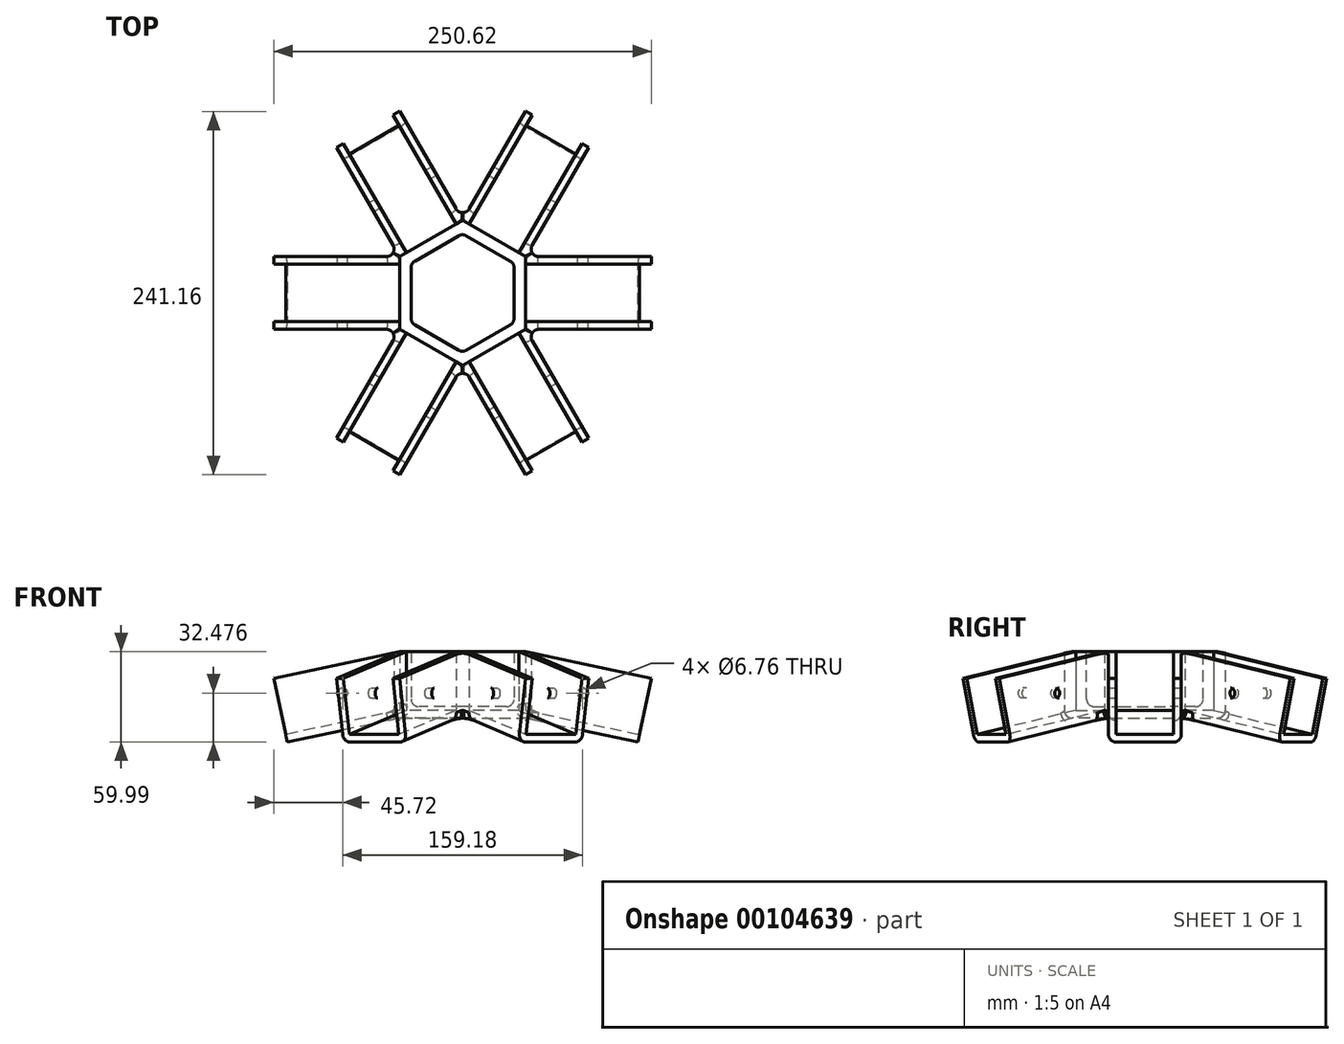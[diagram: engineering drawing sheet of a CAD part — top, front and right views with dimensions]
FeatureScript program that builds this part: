
annotation { "Feature Type Name" : "Feature", "Feature Type Description" : "" }
export const myFeature = defineFeature(function(context is Context, id is Id, definition is map)
    precondition{}
    {
        {
            var Q0;
            Q0=qCreatedBy(makeId("Top.planeOp"),FACE);
            var sketch = newSketch(context, id + "F0", { "sketchPlane" : qUnion([Q0])});
            skCircle(sketch, "E0.cCircle", {"center": v(0, 0) * mm, "radius": 41.8 * mm, "construction": true});
            skLineSegment(sketch, "E0.0", {"start": v(41.8, 24.13) * mm, "end": v(41.8, -24.13) * mm});
            skLineSegment(sketch, "E0.1", {"start": v(41.8, -24.13) * mm, "end": v(0, -48.26) * mm});
            skLineSegment(sketch, "E0.2", {"start": v(0, -48.26) * mm, "end": v(-41.8, -24.13) * mm});
            skLineSegment(sketch, "E0.3", {"start": v(-41.8, -24.13) * mm, "end": v(-41.8, 24.13) * mm});
            skLineSegment(sketch, "E0.4", {"start": v(-41.8, 24.13) * mm, "end": v(0, 48.26) * mm});
            skLineSegment(sketch, "E0.5", {"start": v(0, 48.26) * mm, "end": v(41.8, 24.13) * mm});
            skPoint(sketch, "E0.0.midPoint", {"position": v(41.8, 0) * mm});
            skSolve(sketch);
        }
        {
            var Q0;
            Q0=qSketchRegion(id+"F0",true);
            extrude(context, id + "F1", {"entities" : qUnion([Q0]), "depth" : 44.15 * mm});
        }
        {
            var Q0;
            Q0=qCreatedBy(makeId("Front.planeOp"),FACE);
            var sketch = newSketch(context, id + "F2", { "sketchPlane" : qUnion([Q0])});
            skLineSegment(sketch, "E1", {"start": v(41.8, 0) * mm, "end": v(116.33, -15.84) * mm});
            skLineSegment(sketch, "E2", {"start": v(116.33, -15.84) * mm, "end": v(125.3, 26.4) * mm});
            skLineSegment(sketch, "E3", {"start": v(125.3, 26.4) * mm, "end": v(41.8, 44.15) * mm});
            skLineSegment(sketch, "E4", {"start": v(41.8, 44.15) * mm, "end": v(41.8, 0) * mm});
            skSolve(sketch);
        }
        {
            var Q0;
            Q0=makeQuery(id+"F2.imprint","IMPRINT",FACE,{"disambiguationData":[TD([[makeQuery(id+"F2.imprint","IMPRINT",EDGE,{"derivedFrom":sQuery(id+"F2.wireOp",EDGE,"E1")}),1.0]])]});
            extrude(context, id + "F3", {"entities" : qUnion([Q0]), "endBound" : BoundingType.SYMMETRIC, "depth" : 48.26 * mm});
        }
        {
            var Q0;
            Q0=makeQuery(id+"F3.opExtrude","SWEPT_FACE",FACE,{"disambiguationData":[OSD([sQuery(id+"F2.wireOp",EDGE,"E3")])]});
            var Q1;
            Q1=makeQuery(id+"F3.opExtrude","SWEPT_FACE",FACE,{"disambiguationData":[OSD([sQuery(id+"F2.wireOp",EDGE,"E2")])]});
            var Q2;
            Q2=makeQuery(id+"F3.opExtrude","SWEPT_FACE",FACE,{"disambiguationData":[OSD([sQuery(id+"F2.wireOp",EDGE,"E4")])]});
            shell(context, id + "F4", {"entities" : qUnion([Q0, Q1, Q2]), "thickness" : 5.08 * mm});
        }
        {
            var Q0;
            Q0=makeQuery(id+"F3.opExtrude","CAP_FACE",FACE,{"disambiguationData":[OSD([sQuery(id+"F2.wireOp",EDGE,"E1"),sQuery(id+"F2.wireOp",EDGE,"E2"),sQuery(id+"F2.wireOp",EDGE,"E3"),sQuery(id+"F2.wireOp",EDGE,"E4")])],"isStart":false});
            var sketch = newSketch(context, id + "F5", { "sketchPlane" : qUnion([Q0])});
            skPoint(sketch, "E5", {"position": v(79.59, 16.64) * mm});
            skLineSegment(sketch, "E6", {"start": v(41.8, 44.15) * mm, "end": v(117.39, -10.87) * mm, "construction": true});
            skSolve(sketch);
        }
        {
            var Q0;
            Q0=sQuery(id+"F5.wireOp",VERTEX,"E5");
            var Q1;
            Q1=makeQuery(id+"F3.opExtrude","SWEPT_BODY",BODY,{"disambiguationData":[OSD([sQuery(id+"F2.wireOp",EDGE,"E1"),sQuery(id+"F2.wireOp",EDGE,"E2"),sQuery(id+"F2.wireOp",EDGE,"E3"),sQuery(id+"F2.wireOp",EDGE,"E4")])]});
            hole(context, id + "F6", {"style" : HoleStyle.SIMPLE, "endStyle" : HoleEndStyle.THROUGH, "standardTappedOrClearance" : lookupTablePath({ "standard" : "ANSI", "fit" : "Normal (ASME)", "size" : "1/4", "type" : "Clearance" }), "standardBlindInLast" : lookupTablePath({ "fit" : "Free", "standard" : "ANSI", "size" : "1/4", "type" : "Clearance" }), "holeDiameter" : 6.76 * mm, "locations" : qUnion([Q0]), "scope" : qUnion([Q1]), "isTappedThrough" : true});
        }
        {
            var Q0;
            Q0=qCreatedBy(makeId("Front.planeOp"),FACE);
            var sketch = newSketch(context, id + "F7", { "sketchPlane" : qUnion([Q0])});
            skLineSegment(sketch, "E7", {"start": v(0, 0) * mm, "end": v(0, 66.69) * mm, "construction": true});
            skSolve(sketch);
        }
        {
            var Q0;
            Q0=makeQuery(id+"F1.opExtrude","CAP_FACE",FACE,{"disambiguationData":[OSD([sQuery(id+"F0.wireOp",EDGE,"E0.0"),sQuery(id+"F0.wireOp",EDGE,"E0.1"),sQuery(id+"F0.wireOp",EDGE,"E0.2"),sQuery(id+"F0.wireOp",EDGE,"E0.3"),sQuery(id+"F0.wireOp",EDGE,"E0.4"),sQuery(id+"F0.wireOp",EDGE,"E0.5")])],"isStart":false});
            shell(context, id + "F8", {"entities" : qUnion([Q0]), "thickness" : 7.62 * mm});
        }
        {
            var Q0;
            Q0=makeQuery(id+"F3.opExtrude","SWEPT_BODY",BODY,{"disambiguationData":[OSD([sQuery(id+"F2.wireOp",EDGE,"E1"),sQuery(id+"F2.wireOp",EDGE,"E2"),sQuery(id+"F2.wireOp",EDGE,"E3"),sQuery(id+"F2.wireOp",EDGE,"E4")])]});
            var Q1;
            Q1=sQuery(id+"F7.wireOp",EDGE,"E7");
            circularPattern(context, id + "F9", {"entities" : qUnion([Q0]), "axis" : qUnion([Q1]), "angle" : 60 * degree, "instanceCount" : 6});
        }
        {
            var Q0;
            Q0=makeQuery(id+"F9.opPattern","COPY",BODY,{"derivedFrom":makeQuery(id+"F3.opExtrude","SWEPT_BODY",BODY,{"disambiguationData":[OSD([sQuery(id+"F2.wireOp",EDGE,"E1"),sQuery(id+"F2.wireOp",EDGE,"E2"),sQuery(id+"F2.wireOp",EDGE,"E3"),sQuery(id+"F2.wireOp",EDGE,"E4")])]}),"instanceName":"3"});
            var Q1;
            Q1=makeQuery(id+"F9.opPattern","COPY",BODY,{"derivedFrom":makeQuery(id+"F3.opExtrude","SWEPT_BODY",BODY,{"disambiguationData":[OSD([sQuery(id+"F2.wireOp",EDGE,"E1"),sQuery(id+"F2.wireOp",EDGE,"E2"),sQuery(id+"F2.wireOp",EDGE,"E3"),sQuery(id+"F2.wireOp",EDGE,"E4")])]}),"instanceName":"2"});
            var Q2;
            Q2=makeQuery(id+"F9.opPattern","COPY",BODY,{"derivedFrom":makeQuery(id+"F3.opExtrude","SWEPT_BODY",BODY,{"disambiguationData":[OSD([sQuery(id+"F2.wireOp",EDGE,"E1"),sQuery(id+"F2.wireOp",EDGE,"E2"),sQuery(id+"F2.wireOp",EDGE,"E3"),sQuery(id+"F2.wireOp",EDGE,"E4")])]}),"instanceName":"1"});
            var Q3;
            Q3=makeQuery(id+"F3.opExtrude","SWEPT_BODY",BODY,{"disambiguationData":[OSD([sQuery(id+"F2.wireOp",EDGE,"E1"),sQuery(id+"F2.wireOp",EDGE,"E2"),sQuery(id+"F2.wireOp",EDGE,"E3"),sQuery(id+"F2.wireOp",EDGE,"E4")])]});
            var Q4;
            Q4=makeQuery(id+"F9.opPattern","COPY",BODY,{"derivedFrom":makeQuery(id+"F3.opExtrude","SWEPT_BODY",BODY,{"disambiguationData":[OSD([sQuery(id+"F2.wireOp",EDGE,"E1"),sQuery(id+"F2.wireOp",EDGE,"E2"),sQuery(id+"F2.wireOp",EDGE,"E3"),sQuery(id+"F2.wireOp",EDGE,"E4")])]}),"instanceName":"5"});
            var Q5;
            Q5=makeQuery(id+"F9.opPattern","COPY",BODY,{"derivedFrom":makeQuery(id+"F3.opExtrude","SWEPT_BODY",BODY,{"disambiguationData":[OSD([sQuery(id+"F2.wireOp",EDGE,"E1"),sQuery(id+"F2.wireOp",EDGE,"E2"),sQuery(id+"F2.wireOp",EDGE,"E3"),sQuery(id+"F2.wireOp",EDGE,"E4")])]}),"instanceName":"4"});
            var Q6;
            Q6=makeQuery(id+"F1.opExtrude","SWEPT_BODY",BODY,{"disambiguationData":[OSD([sQuery(id+"F0.wireOp",EDGE,"E0.0"),sQuery(id+"F0.wireOp",EDGE,"E0.1"),sQuery(id+"F0.wireOp",EDGE,"E0.2"),sQuery(id+"F0.wireOp",EDGE,"E0.3"),sQuery(id+"F0.wireOp",EDGE,"E0.4"),sQuery(id+"F0.wireOp",EDGE,"E0.5")])]});
            booleanBodies(context, id + "F10", {"operationType" : BooleanOperationType.UNION, "tools" : qUnion([Q0, Q1, Q2, Q3, Q4, Q5, Q6])});
        }
        {
            var Q0;
            Q0=makeQuery(id+"F8.opShell","OFFSET_EDGE",EDGE,{"disambiguationData":[OSD([sQuery(id+"F0.wireOp",EDGE,"E0.4"),sQuery(id+"F0.wireOp",EDGE,"E0.5")])]});
            var Q1;
            Q1=makeQuery(id+"F8.opShell","OFFSET_EDGE",EDGE,{"disambiguationData":[OSD([sQuery(id+"F0.wireOp",EDGE,"E0.0"),sQuery(id+"F0.wireOp",EDGE,"E0.5")])]});
            var Q2;
            Q2=makeQuery(id+"F8.opShell","OFFSET_EDGE",EDGE,{"disambiguationData":[OSD([sQuery(id+"F0.wireOp",EDGE,"E0.0"),sQuery(id+"F0.wireOp",EDGE,"E0.1")])]});
            var Q3;
            Q3=makeQuery(id+"F8.opShell","OFFSET_EDGE",EDGE,{"disambiguationData":[OSD([sQuery(id+"F0.wireOp",EDGE,"E0.1"),sQuery(id+"F0.wireOp",EDGE,"E0.2")])]});
            var Q4;
            Q4=makeQuery(id+"F8.opShell","OFFSET_EDGE",EDGE,{"disambiguationData":[OSD([sQuery(id+"F0.wireOp",EDGE,"E0.2"),sQuery(id+"F0.wireOp",EDGE,"E0.3")])]});
            var Q5;
            Q5=makeQuery(id+"F8.opShell","OFFSET_EDGE",EDGE,{"disambiguationData":[OSD([sQuery(id+"F0.wireOp",EDGE,"E0.3"),sQuery(id+"F0.wireOp",EDGE,"E0.4")])]});
            fillet(context, id + "F11", {"entities" : qUnion([Q0, Q1, Q2, Q3, Q4, Q5]), "radius" : 5.08 * mm, "tangentPropagation" : true, "allowEdgeOverflow" : false});
        }
        {
            var Q0;
            {var subQ0=sQuery(id+"F2.wireOp",EDGE,"E4");Q0=makeQuery(id+"F10.opBoolean","MERGE",EDGE,{"derivedFrom":[makeQuery(id+"F1.opExtrude","SWEPT_EDGE",EDGE,{"disambiguationData":[OSD([sQuery(id+"F0.wireOp",EDGE,"E0.1"),sQuery(id+"F0.wireOp",EDGE,"E0.2")])]}),makeQuery(id+"F9.opPattern","COPY",EDGE,{"derivedFrom":makeQuery(id+"F3.opExtrude","CAP_EDGE",EDGE,{"disambiguationData":[OSD([subQ0])],"isStart":true}),"instanceName":"4"}),makeQuery(id+"F9.opPattern","COPY",EDGE,{"derivedFrom":makeQuery(id+"F3.opExtrude","CAP_EDGE",EDGE,{"disambiguationData":[OSD([subQ0])],"isStart":false}),"instanceName":"5"})]});}
            var Q1;
            {var subQ0=sQuery(id+"F2.wireOp",EDGE,"E4");Q1=makeQuery(id+"F10.opBoolean","MERGE",EDGE,{"derivedFrom":[makeQuery(id+"F1.opExtrude","SWEPT_EDGE",EDGE,{"disambiguationData":[OSD([sQuery(id+"F0.wireOp",EDGE,"E0.0"),sQuery(id+"F0.wireOp",EDGE,"E0.1")])]}),makeQuery(id+"F3.opExtrude","CAP_EDGE",EDGE,{"disambiguationData":[OSD([subQ0])],"isStart":false}),makeQuery(id+"F9.opPattern","COPY",EDGE,{"derivedFrom":makeQuery(id+"F3.opExtrude","CAP_EDGE",EDGE,{"disambiguationData":[OSD([subQ0])],"isStart":true}),"instanceName":"5"})]});}
            var Q2;
            {var subQ0=sQuery(id+"F2.wireOp",EDGE,"E4");Q2=makeQuery(id+"F10.opBoolean","MERGE",EDGE,{"derivedFrom":[makeQuery(id+"F1.opExtrude","SWEPT_EDGE",EDGE,{"disambiguationData":[OSD([sQuery(id+"F0.wireOp",EDGE,"E0.0"),sQuery(id+"F0.wireOp",EDGE,"E0.5")])]}),makeQuery(id+"F3.opExtrude","CAP_EDGE",EDGE,{"disambiguationData":[OSD([subQ0])],"isStart":true}),makeQuery(id+"F9.opPattern","COPY",EDGE,{"derivedFrom":makeQuery(id+"F3.opExtrude","CAP_EDGE",EDGE,{"disambiguationData":[OSD([subQ0])],"isStart":false}),"instanceName":"1"})]});}
            var Q3;
            {var subQ0=sQuery(id+"F2.wireOp",EDGE,"E4");Q3=makeQuery(id+"F10.opBoolean","MERGE",EDGE,{"derivedFrom":[makeQuery(id+"F1.opExtrude","SWEPT_EDGE",EDGE,{"disambiguationData":[OSD([sQuery(id+"F0.wireOp",EDGE,"E0.4"),sQuery(id+"F0.wireOp",EDGE,"E0.5")])]}),makeQuery(id+"F9.opPattern","COPY",EDGE,{"derivedFrom":makeQuery(id+"F3.opExtrude","CAP_EDGE",EDGE,{"disambiguationData":[OSD([subQ0])],"isStart":true}),"instanceName":"1"}),makeQuery(id+"F9.opPattern","COPY",EDGE,{"derivedFrom":makeQuery(id+"F3.opExtrude","CAP_EDGE",EDGE,{"disambiguationData":[OSD([subQ0])],"isStart":false}),"instanceName":"2"})]});}
            var Q4;
            {var subQ0=sQuery(id+"F2.wireOp",EDGE,"E4");Q4=makeQuery(id+"F10.opBoolean","MERGE",EDGE,{"derivedFrom":[makeQuery(id+"F1.opExtrude","SWEPT_EDGE",EDGE,{"disambiguationData":[OSD([sQuery(id+"F0.wireOp",EDGE,"E0.3"),sQuery(id+"F0.wireOp",EDGE,"E0.4")])]}),makeQuery(id+"F9.opPattern","COPY",EDGE,{"derivedFrom":makeQuery(id+"F3.opExtrude","CAP_EDGE",EDGE,{"disambiguationData":[OSD([subQ0])],"isStart":true}),"instanceName":"2"}),makeQuery(id+"F9.opPattern","COPY",EDGE,{"derivedFrom":makeQuery(id+"F3.opExtrude","CAP_EDGE",EDGE,{"disambiguationData":[OSD([subQ0])],"isStart":false}),"instanceName":"3"})]});}
            var Q5;
            {var subQ0=sQuery(id+"F2.wireOp",EDGE,"E4");Q5=makeQuery(id+"F10.opBoolean","MERGE",EDGE,{"derivedFrom":[makeQuery(id+"F1.opExtrude","SWEPT_EDGE",EDGE,{"disambiguationData":[OSD([sQuery(id+"F0.wireOp",EDGE,"E0.2"),sQuery(id+"F0.wireOp",EDGE,"E0.3")])]}),makeQuery(id+"F9.opPattern","COPY",EDGE,{"derivedFrom":makeQuery(id+"F3.opExtrude","CAP_EDGE",EDGE,{"disambiguationData":[OSD([subQ0])],"isStart":true}),"instanceName":"3"}),makeQuery(id+"F9.opPattern","COPY",EDGE,{"derivedFrom":makeQuery(id+"F3.opExtrude","CAP_EDGE",EDGE,{"disambiguationData":[OSD([subQ0])],"isStart":false}),"instanceName":"4"})]});}
            fillet(context, id + "F12", {"entities" : qUnion([Q0, Q1, Q2, Q3, Q4, Q5]), "radius" : 5.08 * mm, "tangentPropagation" : true, "allowEdgeOverflow" : false});
        }
        {
            var Q0;
            {var subQ0=sQuery(id+"F0.wireOp",EDGE,"E0.3");Q0=makeQuery(id+"F8.opShell","OFFSET_EDGE",EDGE,{"disambiguationData":[OSD([subQ0]),TDD([makeQuery(id+"F1.opExtrude","CAP_EDGE",EDGE,{"disambiguationData":[OSD([subQ0])],"isStart":true})])]});}
            fillet(context, id + "F13", {"entities" : qUnion([Q0]), "radius" : 5.08 * mm, "tangentPropagation" : true, "allowEdgeOverflow" : false});
        }
        {
            var Q0;
            Q0=makeQuery(id+"F9.opPattern","COPY",EDGE,{"derivedFrom":makeQuery(id+"F3.opExtrude","CAP_EDGE",EDGE,{"disambiguationData":[OSD([sQuery(id+"F2.wireOp",EDGE,"E1")])],"isStart":false}),"instanceName":"1"});
            var Q1;
            Q1=makeQuery(id+"F3.opExtrude","CAP_EDGE",EDGE,{"disambiguationData":[OSD([sQuery(id+"F2.wireOp",EDGE,"E1")])],"isStart":true});
            var Q2;
            Q2=makeQuery(id+"F9.opPattern","COPY",EDGE,{"derivedFrom":makeQuery(id+"F3.opExtrude","CAP_EDGE",EDGE,{"disambiguationData":[OSD([sQuery(id+"F2.wireOp",EDGE,"E1")])],"isStart":true}),"instanceName":"1"});
            var Q3;
            Q3=makeQuery(id+"F9.opPattern","COPY",EDGE,{"derivedFrom":makeQuery(id+"F3.opExtrude","CAP_EDGE",EDGE,{"disambiguationData":[OSD([sQuery(id+"F2.wireOp",EDGE,"E1")])],"isStart":false}),"instanceName":"2"});
            var Q4;
            Q4=makeQuery(id+"F9.opPattern","COPY",EDGE,{"derivedFrom":makeQuery(id+"F3.opExtrude","CAP_EDGE",EDGE,{"disambiguationData":[OSD([sQuery(id+"F2.wireOp",EDGE,"E1")])],"isStart":true}),"instanceName":"2"});
            var Q5;
            Q5=makeQuery(id+"F9.opPattern","COPY",EDGE,{"derivedFrom":makeQuery(id+"F3.opExtrude","CAP_EDGE",EDGE,{"disambiguationData":[OSD([sQuery(id+"F2.wireOp",EDGE,"E1")])],"isStart":false}),"instanceName":"3"});
            var Q6;
            Q6=makeQuery(id+"F9.opPattern","COPY",EDGE,{"derivedFrom":makeQuery(id+"F3.opExtrude","CAP_EDGE",EDGE,{"disambiguationData":[OSD([sQuery(id+"F2.wireOp",EDGE,"E1")])],"isStart":true}),"instanceName":"3"});
            var Q7;
            Q7=makeQuery(id+"F9.opPattern","COPY",EDGE,{"derivedFrom":makeQuery(id+"F3.opExtrude","CAP_EDGE",EDGE,{"disambiguationData":[OSD([sQuery(id+"F2.wireOp",EDGE,"E1")])],"isStart":false}),"instanceName":"4"});
            var Q8;
            Q8=makeQuery(id+"F9.opPattern","COPY",EDGE,{"derivedFrom":makeQuery(id+"F3.opExtrude","CAP_EDGE",EDGE,{"disambiguationData":[OSD([sQuery(id+"F2.wireOp",EDGE,"E1")])],"isStart":true}),"instanceName":"4"});
            var Q9;
            Q9=makeQuery(id+"F9.opPattern","COPY",EDGE,{"derivedFrom":makeQuery(id+"F3.opExtrude","CAP_EDGE",EDGE,{"disambiguationData":[OSD([sQuery(id+"F2.wireOp",EDGE,"E1")])],"isStart":false}),"instanceName":"5"});
            var Q10;
            Q10=makeQuery(id+"F3.opExtrude","CAP_EDGE",EDGE,{"disambiguationData":[OSD([sQuery(id+"F2.wireOp",EDGE,"E1")])],"isStart":false});
            var Q11;
            Q11=makeQuery(id+"F9.opPattern","COPY",EDGE,{"derivedFrom":makeQuery(id+"F3.opExtrude","CAP_EDGE",EDGE,{"disambiguationData":[OSD([sQuery(id+"F2.wireOp",EDGE,"E1")])],"isStart":true}),"instanceName":"5"});
            fillet(context, id + "F14", {"entities" : qUnion([Q0, Q1, Q2, Q3, Q4, Q5, Q6, Q7, Q8, Q9, Q10, Q11]), "radius" : 5.08 * mm, "tangentPropagation" : true, "allowEdgeOverflow" : false});
        }
    });
